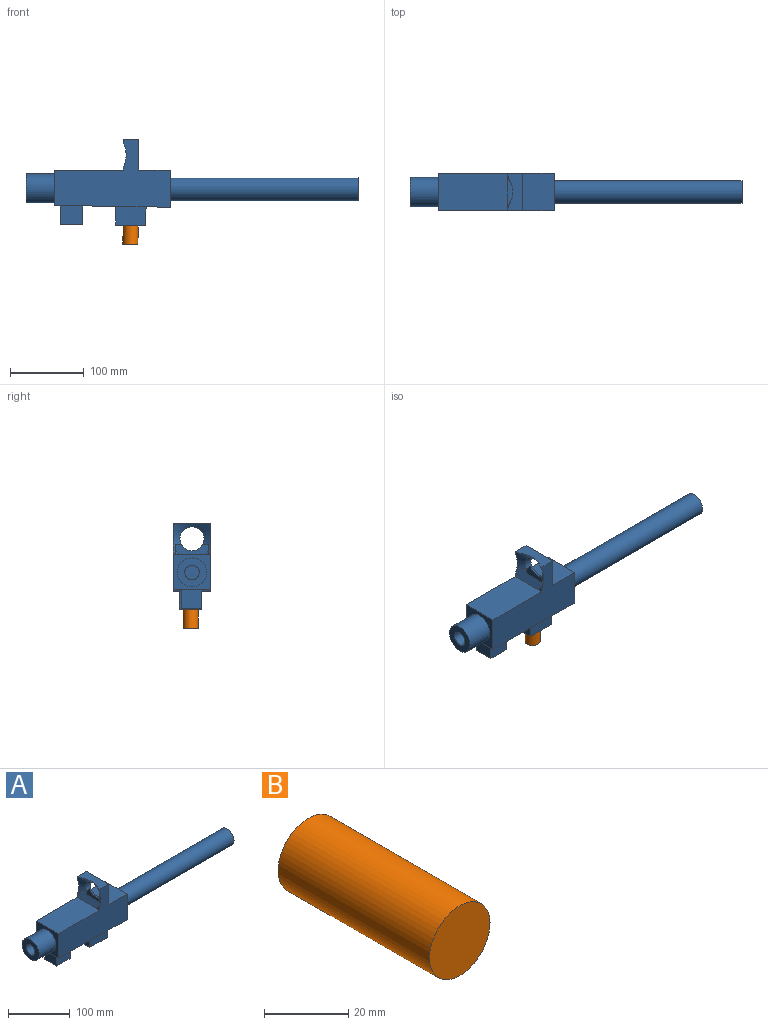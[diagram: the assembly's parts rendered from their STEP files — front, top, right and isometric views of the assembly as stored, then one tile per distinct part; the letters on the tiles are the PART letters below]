
ASSEMBLY  parts=2 mates=1
PART A: 50 faces, bbox 449.4x62.3x126.9 mm
  f0: plane 50.8x50.8mm, normal (0,0,-1), area 1753.3mm2, adj f5,f6,f14,f31,f43,f44,f45,f46
  f1: plane 2.84x2.24mm, normal (-1,0,0), area 3mm2, adj f6,f13,f29
  f2: plane 2.69x2.11mm, normal (-1,0,0), area 2.7mm2, adj f6,f18,f29
  f3: plane 2.69x2.11mm, normal (-1,0,0), area 2.7mm2, adj f5,f18,f29
  f4: plane 2.84x2.24mm, normal (-1,0,0), area 3mm2, adj f5,f13,f29
  f5: plane 156.94x91.25mm, normal (0,-1,0), area 8490.5mm2, adj f0,f3,f4,f13,f14,f15,f16,f17
  f6: plane 156.94x91.25mm, normal (0,1,0), area 8490.5mm2, adj f0,f1,f2,f13,f14,f15,f16,f17
  f7: plane 13.5x8.37mm, normal (0,0,-1), area 90mm2, adj f12,f25,f28,f29
  f8: plane 13.5x8.37mm, normal (0,0,-1), area 90mm2, adj f11,f25,f28,f29
  f9: plane 7.99x7.95mm, normal (1,0,0), area 27.4mm2, adj f10,f11,f29
  f10: plane 46.1x43.02mm, normal (0,0,-1), area 1857.9mm2, adj f9,f11,f12,f21,f26,f29,f30
  f11: plane 101.06x60.74mm, normal (0,1,0), area 4724mm2, adj f8,f9,f10,f21,f22,f23,f24,f25
  f12: plane 101.06x60.74mm, normal (0,-1,0), area 4724mm2, adj f7,f10,f21,f22,f23,f24,f25,f26
  f13: plane 50.8x20.9mm, normal (0,0,1), area 845.6mm2, adj f1,f4,f5,f6,f17,f29
  f14: plane 106.14x50.8mm, normal (-0.02,0,-1), area 4143.9mm2, adj f0,f5,f6,f15,f36,f37,f38,f40
  f15: plane 50.8x50.31mm, normal (1,0,0), area 1803.1mm2, adj f5,f6,f14,f16,f19
  f16: plane 50.8x42.61mm, normal (0,0,1), area 2164.7mm2, adj f5,f6,f15,f17
  f17: plane 50.8x40.95mm, normal (1,0,0), area 1248.3mm2, adj f5,f6,f13,f16,f28
  f18: plane 93.43x50.8mm, normal (0,0,1), area 4746.2mm2, adj f2,f3,f5,f6,f30,f31
  f19: cylinder r=15.48mm len=254mm, axis (-1,0,0), area 24699.7mm2, adj f15,f20
  f20: plane 30.95x30.95mm, normal (1,0,0), area 226.7mm2, adj f19,f27
  f21: plane 45.72x43.63mm, normal (1,0,0), area 1994.7mm2, adj f10,f11,f12,f22
  f22: plane 101.06x45.72mm, normal (0.02,0,1), area 4620.8mm2, adj f11,f12,f21,f23
  f23: plane 45.72x45.19mm, normal (-1,0,0), area 1540.2mm2, adj f11,f12,f22,f24,f27
  f24: plane 45.72x42.61mm, normal (0,0,-1), area 1948.2mm2, adj f11,f12,f23,f25
  f25: plane 45.72x15.55mm, normal (-1,0,0), area 526.9mm2, adj f7,f8,f11,f12,f24,f28
  f26: plane 7.99x7.95mm, normal (1,0,0), area 27.4mm2, adj f10,f12,f29
  f27: cylinder r=12.94mm len=256.54mm, axis (-1,0,0), area 20852.5mm2, adj f20,f23
  f28: cylinder r=16.27mm len=32.54mm, axis (-1,0,0), area 796mm2, adj f7,f8,f17,f25,f29
  f29: cone r=16.27mm half-angle=55deg, axis (-1,0,0), area 1071.9mm2, adj f1,f2,f3,f4,f5,f6,f7,f8
  f30: plane 46.59x2.54mm, normal (1,0,0), area 112.2mm2, adj f10,f18,f29
  f31: plane 50.8x48.67mm, normal (-1,0,0), area 1254.7mm2, adj f0,f5,f6,f18,f33
  f32: cylinder r=9.82mm len=38.1mm, axis (1,0,0), area 2351.9mm2, adj f34,f35
  f33: cylinder r=19.69mm len=39.38mm, axis (1,0,0), area 4713.2mm2, adj f31,f34
  f34: plane 39.38x39.38mm, normal (-1,0,0), area 914.6mm2, adj f32,f33
  f35: plane 19.65x19.65mm, normal (-1,0,0), area 303.2mm2, adj f32
  f36: plane 41.18x26.03mm, normal (0,-1,0), area 1036.2mm2, adj f14,f37,f40,f41
  f37: plane 30.6x25.4mm, normal (-1,0,0.02), area 777.3mm2, adj f14,f36,f38,f41
  f38: plane 41.18x26.03mm, normal (0,1,0), area 1036.2mm2, adj f14,f37,f40,f41
  f39: cylinder r=10.15mm len=25.71mm, axis (0.02,0,1), area 1620.6mm2, adj f41,f42
  f40: plane 30.6x25.4mm, normal (1,0,-0.02), area 777.3mm2, adj f14,f36,f38,f41
  f41: plane 40.79x30.6mm, normal (-0.02,0,-1), area 924.5mm2, adj f36,f37,f38,f39,f40
  f42: plane 20.31x20.31mm, normal (-0.02,0,-1), area 324mm2, adj f39
  f43: plane 27.28x25.4mm, normal (1,0,0), area 693mm2, adj f0,f44,f46,f48
  f44: plane 30.32x25.4mm, normal (0,-1,0), area 770.2mm2, adj f0,f43,f45,f48
  f45: plane 27.28x25.4mm, normal (-1,0,0), area 693mm2, adj f0,f44,f46,f48
  f46: plane 30.32x25.4mm, normal (0,1,0), area 770.2mm2, adj f0,f43,f45,f48
  f47: cylinder r=9.95mm len=25.4mm, axis (0,0,1), area 1587.6mm2, adj f48,f49
  f48: plane 30.32x27.28mm, normal (0,0,-1), area 516.4mm2, adj f43,f44,f45,f46,f47
  f49: plane 19.9x19.9mm, normal (0,0,-1), area 310.9mm2, adj f47
PART B: 3 faces, bbox 20.3x50.8x20.3 mm
  f0: cylinder r=10.16mm len=50.8mm, axis (0,1,0), area 3242.9mm2, adj f1,f2
  f1: plane 20.32x20.32mm, normal (0,-1,0), area 324.3mm2, adj f0
  f2: plane 20.32x20.32mm, normal (0,1,0), area 324.3mm2, adj f0
PLACE A at identity
PLACE B rot(axis=(-1,0.01,0.01),90deg) t=(9.65,-23.48,-100.28)mm
MATE slider B.f0 <-> A.f39  axis (-0.02,0,-1) through (10.44,-23.48,-49.49)mm
